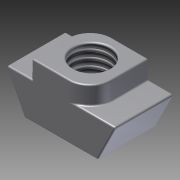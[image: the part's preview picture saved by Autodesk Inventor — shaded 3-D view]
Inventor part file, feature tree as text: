
AUTODESK INVENTOR PART (.ipt)
format: ipt  version: 2011 (Build 150239000, 239)  size: 175,616 bytes
history: native  units: in
note: dims shown in document units (in); Inventor stores cm internally (conversion verified against a paired STEP export)
features: extrude x2, fillet x2, sketch x2, thread x1
ambient origin geometry x8: Origin, YZ Plane, XZ Plane, XY Plane, X Axis, Y Axis, Z Axis, Center Point
bodies: Solid1 (feature_tree)
feature tree (7):
  extrude  "Extrusion1"  Depth=0.75in
  extrude  "Extrusion2"  Depth=0.125in
  fillet  "Fillet1"  Radius=0.4in
  fillet  "Fillet2"  Radius=0.125in
  thread  "Thread1"  [1 undecoded]
  sketch  "Sketch1"  dims[d0=0.25in d1=0.75in]
  sketch  "Sketch2"  dims[d2=0.5in d3=0.125in d4=0.4in d5=0.125in d6=0.175in d7=0.4in d8=0.0in d9=0.25in d10=1.0in d11=0.0in d12=0.15in d13=0.01in d14=1.0in d15=0.0in]
note: 1 required parameter value undecoded (feature->parameter linkage not recoverable at this tier; creation-order binding heuristic only, values carry confidence <= 0.55)
